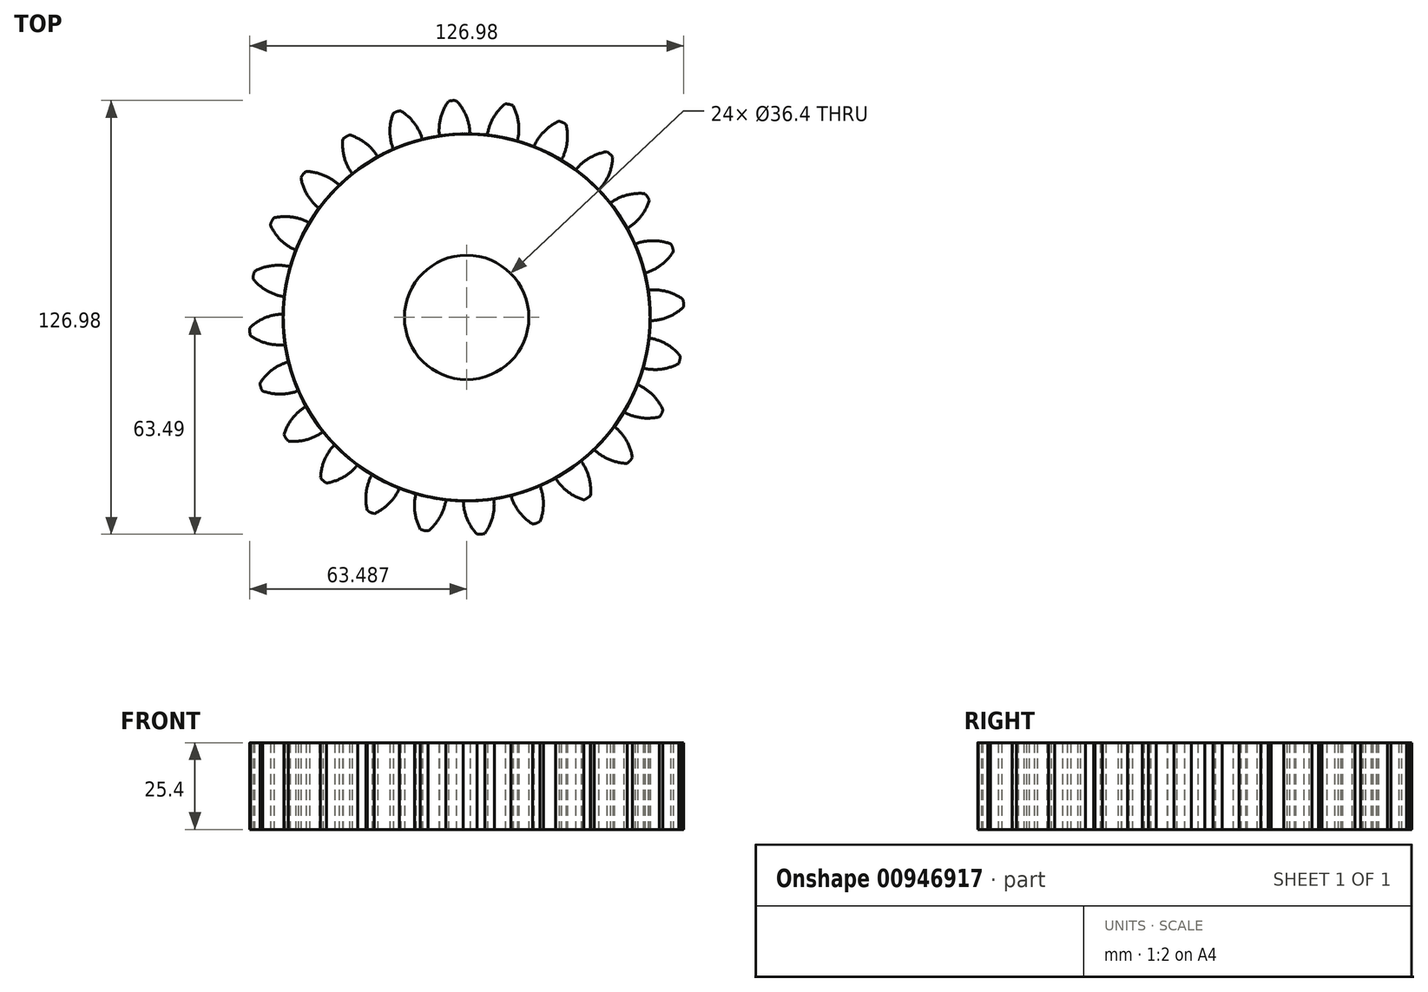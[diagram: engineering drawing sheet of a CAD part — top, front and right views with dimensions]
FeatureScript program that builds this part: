
annotation { "Feature Type Name" : "Feature", "Feature Type Description" : "" }
export const myFeature = defineFeature(function(context is Context, id is Id, definition is map)
    precondition{}
    {
        {
            var Q0;
            Q0=qCreatedBy(makeId("Top.planeOp"),FACE);
            var sketch = newSketch(context, id + "F0", { "sketchPlane" : qUnion([Q0])});
            skCircle(sketch, "E0", {"center": v(0.07, 0) * mm, "radius": 53.72 * mm});
            skCircle(sketch, "E1", {"center": v(0.07, 0) * mm, "radius": 58.67 * mm, "construction": true});
            skCircle(sketch, "E2", {"center": v(0.07, 0) * mm, "radius": 63.5 * mm, "construction": true});
            skLineSegment(sketch, "E3", {"start": v(0.07, 0) * mm, "end": v(0.07, 84.47) * mm, "construction": true});
            skLineSegment(sketch, "E4", {"start": v(0.07, 0) * mm, "end": v(-107.68, 0) * mm, "construction": true});
            skLineSegment(sketch, "E5", {"start": v(0.07, 0) * mm, "end": v(92.28, 0) * mm, "construction": true});
            skLineSegment(sketch, "E6", {"start": v(0.07, 0) * mm, "end": v(-7.02, 108.19) * mm, "construction": true});
            skLineSegment(sketch, "E7", {"start": v(0.07, 58.67) * mm, "end": v(-75.2, 58.67) * mm, "construction": true});
            skLineSegment(sketch, "E8", {"start": v(0.07, 58.67) * mm, "end": v(-66.59, 34.41) * mm, "construction": true});
            skCircle(sketch, "E9", {"center": v(0.07, 0) * mm, "radius": 55.14 * mm, "construction": true});
            skCircle(sketch, "E10", {"center": v(0.07, 58.67) * mm, "radius": 14.6 * mm, "construction": true});
            skCircle(sketch, "E11", {"center": v(-13.56, 53.42) * mm, "radius": 14.6 * mm, "construction": true});
            skArc(sketch, "E12", {"start": v(0.07, 58.67) * mm, "mid": v(-1.2, 61.2) * mm, "end": v(-2.92, 63.43) * mm});
            skArc(sketch, "E13", {"start": v(-2.92, 63.43) * mm, "mid": v(-4.1, 63.48) * mm, "end": v(-5.25, 63.28) * mm});
            skArc(sketch, "E14", {"start": v(1.04, 53.71) * mm, "mid": v(0.77, 56.24) * mm, "end": v(0.07, 58.67) * mm});
            skArc(sketch, "E15.MirrorCS", {"start": v(-7.6, 58.17) * mm, "mid": v(-6.67, 60.84) * mm, "end": v(-5.25, 63.28) * mm});
            skArc(sketch, "E16.MirrorCS", {"start": v(-7.9, 53.13) * mm, "mid": v(-7.97, 55.66) * mm, "end": v(-7.6, 58.17) * mm});
            skCircle(sketch, "E17", {"center": v(0.07, 0) * mm, "radius": 18.2 * mm});
            skSolve(sketch);
        }
        {
            var Q0;
            Q0=makeQuery(id+"F0.imprint","IMPRINT",FACE,{"disambiguationData":[TD([[makeQuery(id+"F0.imprint","IMPRINT",EDGE,{"derivedFrom":sQuery(id+"F0.wireOp",EDGE,"E17")}),-1.0]])]});
            var Q1;
            Q1=makeQuery(id+"F0.imprint","IMPRINT",FACE,{"disambiguationData":[TD([[makeQuery(id+"F0.imprint","IMPRINT",EDGE,{"derivedFrom":sQuery(id+"F0.wireOp",EDGE,"E12")}),1.0]])]});
            extrude(context, id + "F1", {"entities" : qUnion([Q0, Q1]), "endBound" : BoundingType.SYMMETRIC, "depth" : 25.4 * mm, "offsetDistance" : 25.4 * mm});
        }
        {
            var Q0;
            Q0=makeQuery(id+"F1.opExtrude","SWEPT_BODY",BODY,{"disambiguationData":[OSD([sQuery(id+"F0.wireOp",EDGE,"E0"),sQuery(id+"F0.wireOp",EDGE,"E12"),sQuery(id+"F0.wireOp",EDGE,"E13"),sQuery(id+"F0.wireOp",EDGE,"E14"),sQuery(id+"F0.wireOp",EDGE,"E15.MirrorCS"),sQuery(id+"F0.wireOp",EDGE,"E16.MirrorCS"),sQuery(id+"F0.wireOp",EDGE,"E17")])]});
            var Q1;
            Q1=makeQuery(id+"F1.opExtrude","SWEPT_FACE",FACE,{"disambiguationData":[OSD([sQuery(id+"F0.wireOp",EDGE,"E0")])]});
            circularPattern(context, id + "F2", {"entities" : qUnion([Q0]), "axis" : qUnion([Q1]), "angle" : 360 * degree, "instanceCount" : 24, "equalSpace" : true});
        }
    });
